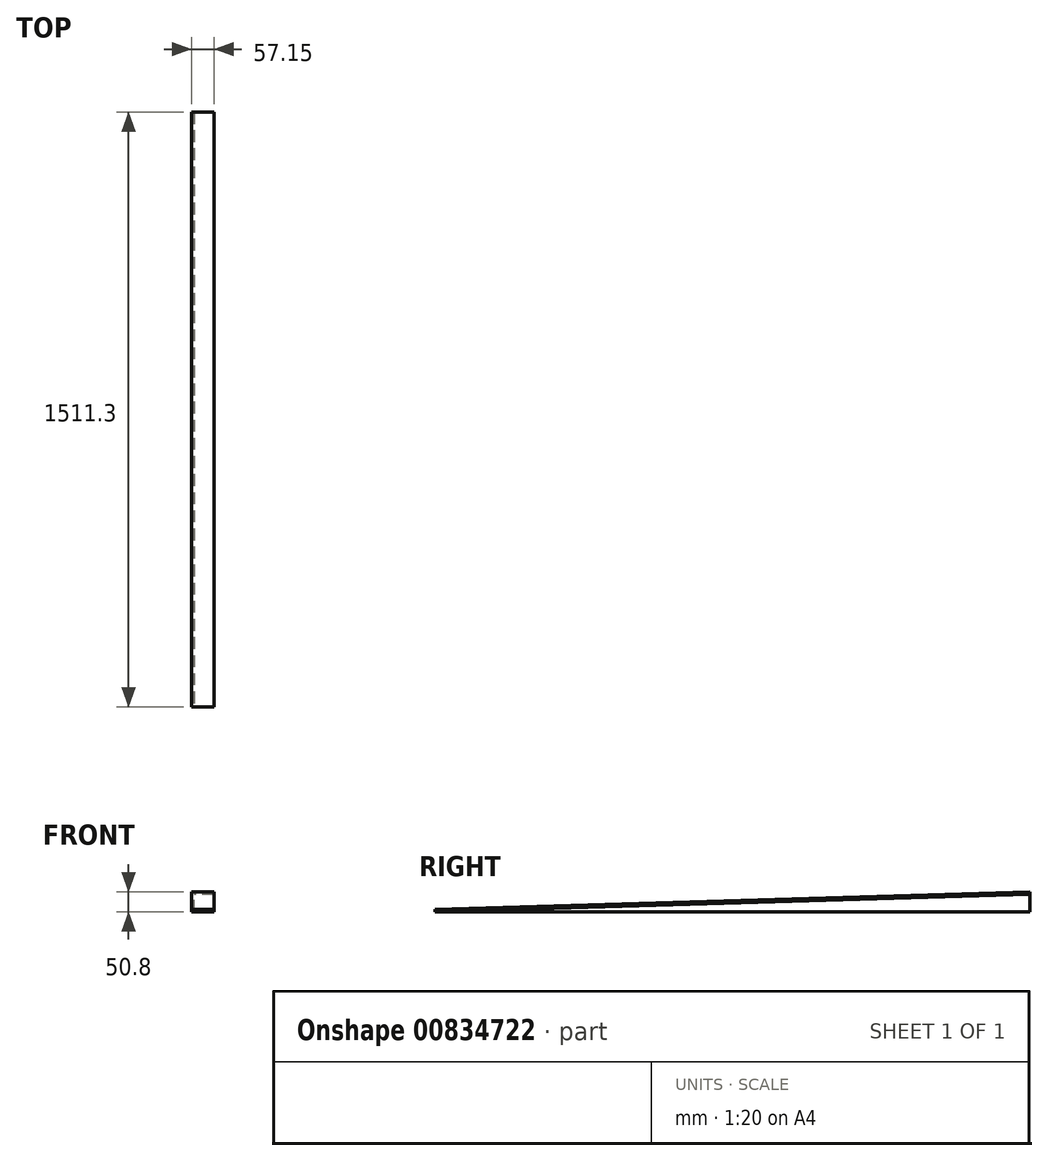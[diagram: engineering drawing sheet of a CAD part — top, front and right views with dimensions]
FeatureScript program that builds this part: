
annotation { "Feature Type Name" : "Feature", "Feature Type Description" : "" }
export const myFeature = defineFeature(function(context is Context, id is Id, definition is map)
    precondition{}
    {
        {
            var Q0;
            Q0=qCreatedBy(makeId("Right.planeOp"),FACE);
            var sketch = newSketch(context, id + "F0", { "sketchPlane" : qUnion([Q0])});
            skLineSegment(sketch, "E0", {"start": v(763, -6.35) * mm, "end": v(-748.3, -6.35) * mm});
            skLineSegment(sketch, "E1", {"start": v(763, -6.35) * mm, "end": v(763, 44.45) * mm});
            skLineSegment(sketch, "E2", {"start": v(-748.3, -6.35) * mm, "end": v(-748.3, 0) * mm});
            skLineSegment(sketch, "E3", {"start": v(763, 44.45) * mm, "end": v(-748.3, 0) * mm});
            skSolve(sketch);
        }
        {
            var Q0;
            Q0 = qSketchRegion(id + "F0", true);
            extrude(context, id + "F1", {"entities" : qUnion([Q0]), "depth" : 6.35 * mm, "offsetDistance" : 25.4 * mm});
        }
        {
            var Q0;
            Q0=makeQuery(id+"F1.opExtrude","CAP_FACE",FACE,{"disambiguationData":[OSD([sQuery(id+"F0.wireOp",EDGE,"E0"),sQuery(id+"F0.wireOp",EDGE,"E1"),sQuery(id+"F0.wireOp",EDGE,"E2"),sQuery(id+"F0.wireOp",EDGE,"E3")])],"isStart":false});
            var sketch = newSketch(context, id + "F2", { "sketchPlane" : qUnion([Q0])});
            skLineSegment(sketch, "E4", {"start": v(763, -6.35) * mm, "end": v(756.65, -6.35) * mm});
            skLineSegment(sketch, "E5", {"start": v(763, -6.35) * mm, "end": v(763, 44.45) * mm});
            skLineSegment(sketch, "E6", {"start": v(763, 44.45) * mm, "end": v(-748.3, 0) * mm});
            skLineSegment(sketch, "E7", {"start": v(-748.3, 0) * mm, "end": v(-748.3, -6.35) * mm});
            skLineSegment(sketch, "E8", {"start": v(-748.3, -6.35) * mm, "end": v(763, 38.1) * mm});
            skLineSegment(sketch, "E9", {"start": v(763, 38.1) * mm, "end": v(763, 44.45) * mm});
            skSolve(sketch);
        }
        {
            var Q0;
            Q0 = qSketchRegion(id + "F2", true);
            extrude(context, id + "F3", {"entities" : qUnion([Q0]), "operationType" : NewBodyOperationType.ADD, "depth" : 50.8 * mm, "offsetDistance" : 25.4 * mm});
        }
    });
